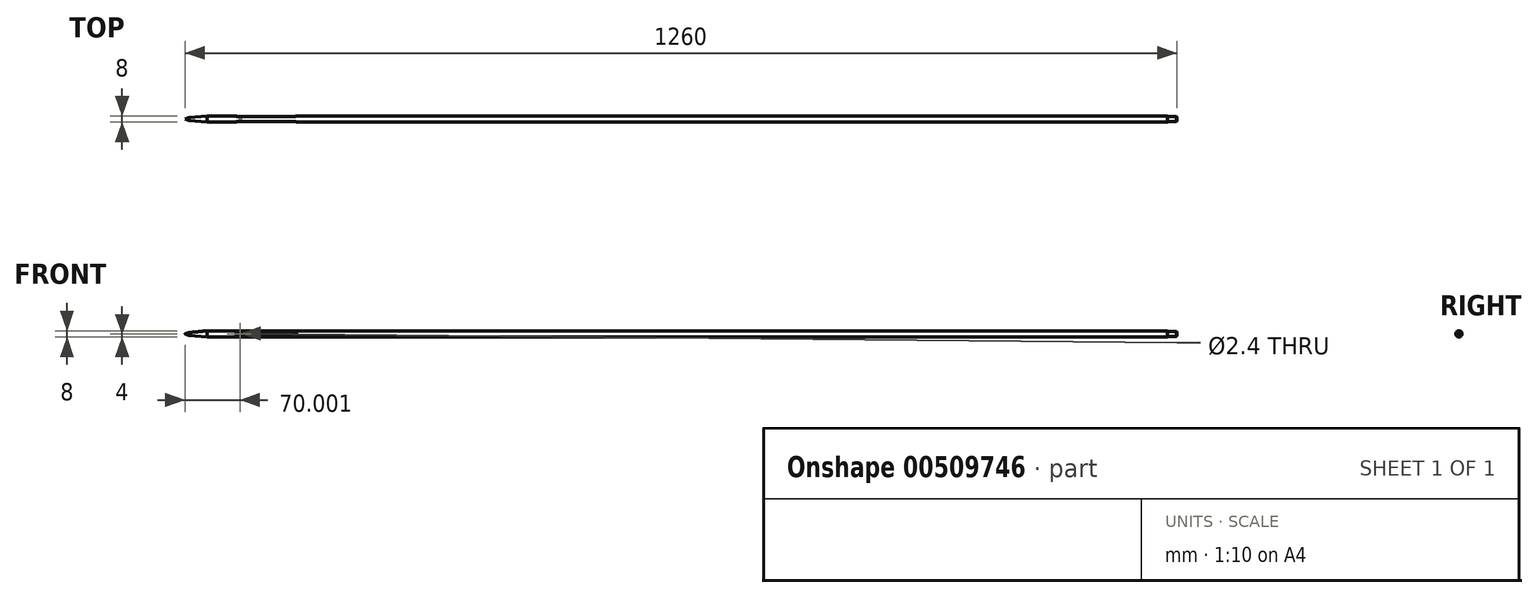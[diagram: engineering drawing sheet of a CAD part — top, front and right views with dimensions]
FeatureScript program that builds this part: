
annotation { "Feature Type Name" : "Feature", "Feature Type Description" : "" }
export const myFeature = defineFeature(function(context is Context, id is Id, definition is map)
    precondition{}
    {
        {
            var Q0;
            Q0=qCreatedBy(makeId("Right.planeOp"),FACE);
            var sketch = newSketch(context, id + "F0", { "sketchPlane" : qUnion([Q0])});
            skCircle(sketch, "E0", {"center": v(0, 0) * mm, "radius": 4 * mm});
            skSolve(sketch);
        }
        {
            var Q0;
            Q0=qSketchRegion(id+"F0",true);
            extrude(context, id + "F1", {"entities" : qUnion([Q0]), "depth" : 1220 * mm});
        }
        {
            var Q0;
            Q0=makeQuery(id+"F1.opExtrude","CAP_FACE",FACE,{"disambiguationData":[OSD([sQuery(id+"F0.wireOp",EDGE,"E0")])],"isStart":false});
            var sketch = newSketch(context, id + "F2", { "sketchPlane" : qUnion([Q0])});
            skCircle(sketch, "E1", {"center": v(0, 0) * mm, "radius": 3 * mm});
            skSolve(sketch);
        }
        {
            var Q0;
            Q0=qSketchRegion(id+"F2",true);
            extrude(context, id + "F3", {"entities" : qUnion([Q0]), "operationType" : NewBodyOperationType.ADD, "depth" : 12 * mm});
        }
        {
            var Q0;
            Q0=makeQuery(id+"F3.opExtrude","CAP_EDGE",EDGE,{"disambiguationData":[OSD([sQuery(id+"F2.wireOp",EDGE,"E1")])],"isStart":false});
            chamfer(context, id + "F4", {"entities" : qUnion([Q0]), "width" : .75 * mm, "tangentPropagation" : true});
        }
        {
            var Q0;
            Q0=makeQuery(id+"F1.opExtrude","CAP_FACE",FACE,{"disambiguationData":[OSD([sQuery(id+"F0.wireOp",EDGE,"E0")])],"isStart":true});
            var sketch = newSketch(context, id + "F5", { "sketchPlane" : qUnion([Q0])});
            skCircle(sketch, "E2", {"center": v(0, 0) * mm, "radius": 4.12 * mm});
            skSolve(sketch);
        }
        {
            var Q0;
            Q0=makeQuery(id+"F5.imprint","IMPRINT",FACE,{"disambiguationData":[TD([[makeQuery(id+"F5.imprint","IMPRINT",EDGE,{"derivedFrom":makeQuery(id+"F1.opExtrude","CAP_EDGE",EDGE,{"disambiguationData":[OSD([sQuery(id+"F0.wireOp",EDGE,"E0")])],"isStart":true})}),-1.0]])]});
            extrude(context, id + "F6", {"entities" : qUnion([Q0]), "operationType" : NewBodyOperationType.ADD, "depth" : 23 * mm, "hasDraft" : true, "draftAngle" : 5.8 * degree, "draftPullDirection" : true});
        }
        {
            var Q0;
            Q0=makeQuery(id+"F6.opExtrude","CAP_FACE",FACE,{"disambiguationData":[OSD([sQuery(id+"F0.wireOp",EDGE,"E0")])],"isStart":false});
            var sketch = newSketch(context, id + "F7", { "sketchPlane" : qUnion([Q0])});
            skCircle(sketch, "E3", {"center": v(0, 0) * mm, "radius": 1.99 * mm});
            skSolve(sketch);
        }
        {
            var Q0;
            Q0=makeQuery(id+"F7.imprint","IMPRINT",FACE,{"disambiguationData":[TD([[makeQuery(id+"F7.imprint","IMPRINT",EDGE,{"derivedFrom":makeQuery(id+"F6.opExtrude","CAP_EDGE",EDGE,{"disambiguationData":[OSD([sQuery(id+"F0.wireOp",EDGE,"E0")])],"isStart":false})}),-1.0]])]});
            extrude(context, id + "F8", {"entities" : qUnion([Q0]), "operationType" : NewBodyOperationType.ADD, "depth" : 5 * mm, "hasDraft" : true, "draftAngle" : 18.3 * degree, "draftPullDirection" : true});
        }
        {
            var Q0;
            Q0=makeQuery(id+"F1.opExtrude","SWEPT_BODY",BODY,{"disambiguationData":[OSD([sQuery(id+"F0.wireOp",EDGE,"E0")])]});
            var Q1;
            Q1=makeQuery(id+"F6.opExtrude","SWEPT_BODY",BODY,{"disambiguationData":[OSD([sQuery(id+"F0.wireOp",EDGE,"E0")])]});
            transform(context, id + "F9", {"entities" : qUnion([Q0, Q1]), "transformType" : TransformType.TRANSLATION_3D, "dx" : 28 * mm, "dy" : 0 * mm, "dz" : 0 * mm, "makeCopy" : false});
        }
        {
            var Q0;
            Q0=qCreatedBy(makeId("Top.planeOp"),FACE);
            var sketch = newSketch(context, id + "F10", { "sketchPlane" : qUnion([Q0])});
            skLineSegment(sketch, "E4", {"start": v(65, 7.56) * mm, "end": v(65, -10.12) * mm, "construction": true});
            skSolve(sketch);
        }
        {
            var Q0;
            Q0=qCreatedBy(makeId("Top.planeOp"),FACE);
            var sketch = newSketch(context, id + "F11", { "sketchPlane" : qUnion([Q0])});
            skLineSegment(sketch, "E5", {"start": v(142, 6.8) * mm, "end": v(142, -11.63) * mm, "construction": true});
            skSolve(sketch);
        }
        {
            var Q0;
            Q0=qCreatedBy(makeId("Top.planeOp"),FACE);
            var sketch = newSketch(context, id + "F12", { "sketchPlane" : qUnion([Q0])});
            skPoint(sketch, "E6.middle", {"position": v(65.03, 0) * mm});
            skLineSegment(sketch, "E7.bottom", {"start": v(141.96, 3.1) * mm, "end": v(64.96, 3.1) * mm});
            skLineSegment(sketch, "E7.top", {"start": v(141.96, -3.1) * mm, "end": v(64.96, -3.1) * mm});
            skLineSegment(sketch, "E7.left", {"start": v(141.96, 3.1) * mm, "end": v(141.96, -3.1) * mm});
            skLineSegment(sketch, "E7.right", {"start": v(64.96, 3.1) * mm, "end": v(64.96, -3.1) * mm});
            skPoint(sketch, "E7.middle", {"position": v(103.46, 0) * mm});
            skSolve(sketch);
        }
        {
            var Q0;
            Q0=qCreatedBy(makeId("Top.planeOp"),FACE);
            var sketch = newSketch(context, id + "F13", { "sketchPlane" : qUnion([Q0])});
            skLineSegment(sketch, "E8", {"start": v(138, 7.3) * mm, "end": v(138, -12.2) * mm, "construction": true});
            skSolve(sketch);
        }
        {
            var Q0;
            Q0=qCreatedBy(makeId("Top.planeOp"),FACE);
            var sketch = newSketch(context, id + "F14", { "sketchPlane" : qUnion([Q0])});
            skLineSegment(sketch, "E9.bottom", {"start": v(65, 3.1) * mm, "end": v(138, 3.1) * mm});
            skLineSegment(sketch, "E9.top", {"start": v(65, 11.8) * mm, "end": v(138, 11.8) * mm});
            skLineSegment(sketch, "E9.left", {"start": v(65, 3.1) * mm, "end": v(65, 11.8) * mm});
            skLineSegment(sketch, "E9.right", {"start": v(138, 3.1) * mm, "end": v(138, 11.8) * mm});
            skLineSegment(sketch, "E10.bottom", {"start": v(65, -8.52) * mm, "end": v(138, -8.52) * mm});
            skLineSegment(sketch, "E10.top", {"start": v(65, -3.1) * mm, "end": v(138, -3.1) * mm});
            skLineSegment(sketch, "E10.left", {"start": v(65, -8.52) * mm, "end": v(65, -3.1) * mm});
            skLineSegment(sketch, "E10.right", {"start": v(138, -8.52) * mm, "end": v(138, -3.1) * mm});
            skSolve(sketch);
        }
        {
            var Q0;
            Q0=qSketchRegion(id+"F14",true);
            extrude(context, id + "F15", {"entities" : qUnion([Q0]), "operationType" : NewBodyOperationType.REMOVE, "oppositeDirection" : true, "depth" : 25 * mm, "hasSecondDirection" : true, "secondDirectionOppositeDirection" : false, "secondDirectionDepth" : 25 * mm});
        }
        {
            var Q0;
            Q0=qCreatedBy(makeId("Front.planeOp"),FACE);
            var sketch = newSketch(context, id + "F16", { "sketchPlane" : qUnion([Q0])});
            skCircle(sketch, "E11", {"center": v(70, 0) * mm, "radius": 1.2 * mm});
            skSolve(sketch);
        }
        {
            var Q0;
            Q0=qSketchRegion(id+"F16",true);
            extrude(context, id + "F17", {"entities" : qUnion([Q0]), "operationType" : NewBodyOperationType.REMOVE, "oppositeDirection" : true, "depth" : 25 * mm, "hasSecondDirection" : true, "secondDirectionOppositeDirection" : false, "secondDirectionDepth" : 25 * mm});
        }
        {
            var Q0;
            Q0=qCreatedBy(makeId("Top.planeOp"),FACE);
            var sketch = newSketch(context, id + "F18", { "sketchPlane" : qUnion([Q0])});
            skLineSegment(sketch, "E12", {"start": v(138, -3.1) * mm, "end": v(142, -3.65) * mm});
            skLineSegment(sketch, "E13", {"start": v(142.03, -3.65) * mm, "end": v(142.23, -3.65) * mm, "construction": true});
            skSolve(sketch);
        }
        {
            var Q0;
            Q0=qCreatedBy(makeId("Top.planeOp"),FACE);
            var sketch = newSketch(context, id + "F19", { "sketchPlane" : qUnion([Q0])});
            skLineSegment(sketch, "E14", {"start": v(138, -3.1) * mm, "end": v(142, -3.65) * mm});
            skLineSegment(sketch, "E15", {"start": v(142, -3.65) * mm, "end": v(142, -4.27) * mm});
            skLineSegment(sketch, "E16", {"start": v(142, -4.27) * mm, "end": v(138, -4.27) * mm});
            skLineSegment(sketch, "E17", {"start": v(138, -4.27) * mm, "end": v(138, -3.1) * mm});
            skLineSegment(sketch, "E18", {"start": v(138, 3.1) * mm, "end": v(142, 3.65) * mm});
            skLineSegment(sketch, "E19", {"start": v(142, 3.65) * mm, "end": v(142, 4.31) * mm});
            skLineSegment(sketch, "E20", {"start": v(142, 4.31) * mm, "end": v(138, 4.31) * mm});
            skLineSegment(sketch, "E21", {"start": v(138, 4.31) * mm, "end": v(138, 3.1) * mm});
            skSolve(sketch);
        }
        {
            var Q0;
            Q0=makeQuery(id+"F19.imprint","IMPRINT",FACE,{"disambiguationData":[TD([[makeQuery(id+"F19.imprint","IMPRINT",EDGE,{"derivedFrom":sQuery(id+"F19.wireOp",EDGE,"E14")}),-1.0]])]});
            var Q1;
            Q1=makeQuery(id+"F19.imprint","IMPRINT",FACE,{"disambiguationData":[TD([[makeQuery(id+"F19.imprint","IMPRINT",EDGE,{"derivedFrom":sQuery(id+"F19.wireOp",EDGE,"E18")}),1.0]])]});
            extrude(context, id + "F20", {"entities" : qUnion([Q0, Q1]), "operationType" : NewBodyOperationType.REMOVE, "oppositeDirection" : true, "depth" : 25 * mm, "hasSecondDirection" : true, "secondDirectionOppositeDirection" : false, "secondDirectionDepth" : 25 * mm});
        }
    });
